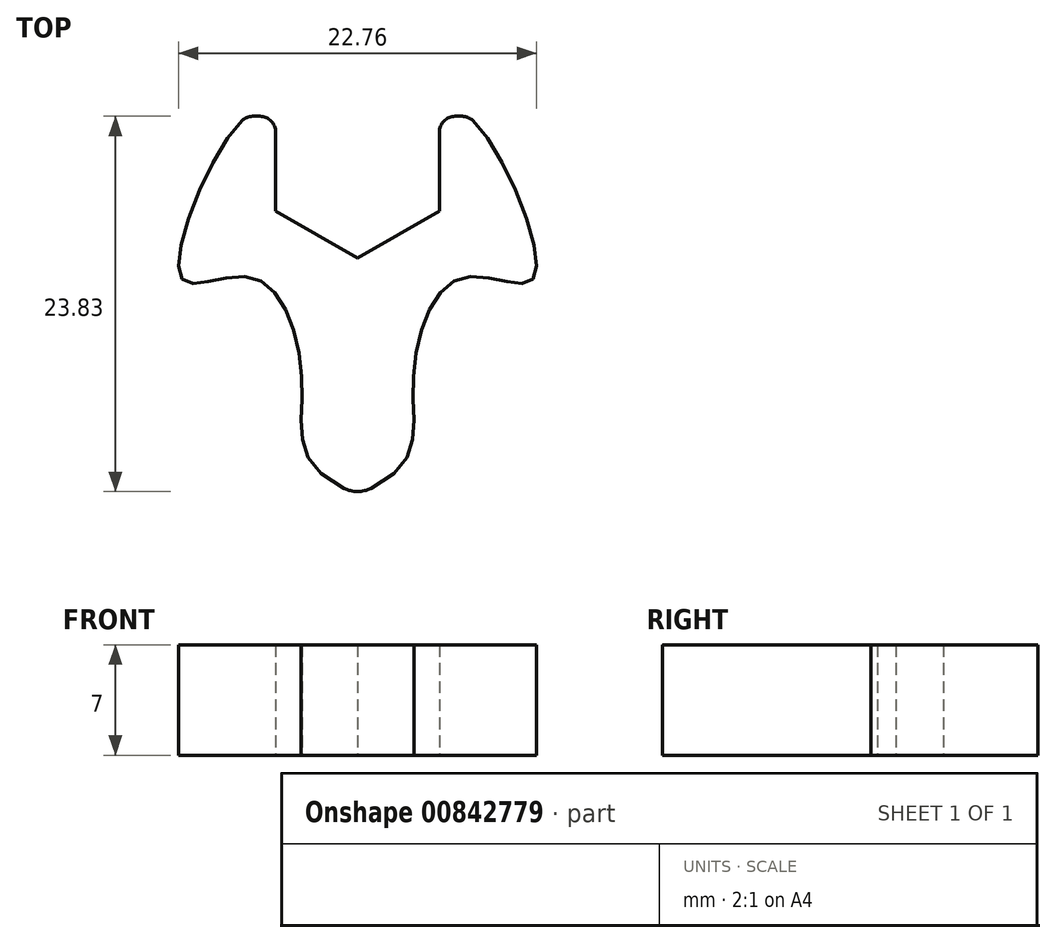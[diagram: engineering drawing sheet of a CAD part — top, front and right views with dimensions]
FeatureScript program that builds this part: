
annotation { "Feature Type Name" : "Feature", "Feature Type Description" : "" }
export const myFeature = defineFeature(function(context is Context, id is Id, definition is map)
    precondition{}
    {
        {
            var Q0;
            Q0=qCreatedBy(makeId("Top.planeOp"),FACE);
            var sketch = newSketch(context, id + "F0", { "sketchPlane" : qUnion([Q0])});
            skCircle(sketch, "E0.cCircle", {"center": v(0, 0) * mm, "radius": 5 * mm, "construction": true});
            skLineSegment(sketch, "E0.0", {"start": v(0, 5.77) * mm, "end": v(5, 2.89) * mm, "construction": true});
            skLineSegment(sketch, "E0.1", {"start": v(5, 2.89) * mm, "end": v(5, -2.89) * mm, "construction": true});
            skLineSegment(sketch, "E0.2", {"start": v(5, -2.89) * mm, "end": v(0, -5.77) * mm, "construction": true});
            skLineSegment(sketch, "E0.3", {"start": v(0, -5.77) * mm, "end": v(-5, -2.89) * mm, "construction": true});
            skLineSegment(sketch, "E0.4", {"start": v(-5, -2.89) * mm, "end": v(-5, 2.89) * mm, "construction": true});
            skLineSegment(sketch, "E0.5", {"start": v(-5, 2.89) * mm, "end": v(0, 5.77) * mm, "construction": true});
            skPoint(sketch, "E0.0.midPoint", {"position": v(2.5, 4.33) * mm});
            skLineSegment(sketch, "E1.0", {"start": v(-5.2, -3) * mm, "end": v(-5.2, 3) * mm, "construction": true});
            skLineSegment(sketch, "E1.1", {"start": v(0, 6) * mm, "end": v(5.2, 3) * mm, "construction": true});
            skLineSegment(sketch, "E1.2", {"start": v(5.2, 3) * mm, "end": v(5.2, -3) * mm});
            skLineSegment(sketch, "E1.3", {"start": v(-5.2, 3) * mm, "end": v(0, 6) * mm, "construction": true});
            skLineSegment(sketch, "E1.4", {"start": v(5.2, -3) * mm, "end": v(0, -6) * mm});
            skLineSegment(sketch, "E1.5", {"start": v(0, -6) * mm, "end": v(-5.2, -3) * mm, "construction": true});
            skLineSegment(sketch, "E2", {"start": v(11.2, -7.25) * mm, "end": v(6.7, -7.25) * mm, "construction": true});
            skLineSegment(sketch, "E3", {"start": v(6.7, -7.25) * mm, "end": v(0, -14.1) * mm, "construction": true});
            skLineSegment(sketch, "E4", {"start": v(5.2, 3) * mm, "end": v(7, 3) * mm});
            skLineSegment(sketch, "E5", {"start": v(7, 3) * mm, "end": v(11.2, -7.25) * mm, "construction": true});
            skFitSpline(sketch, "E6", {"points": [v(5.2, 3) * mm, v(7, 3) * mm, v(11.2, -7.25) * mm, v(6.7, -7.25) * mm, v(3.53, -14.1) * mm, v(0, -21) * mm], "startDerivative": vector(9.76, 6.58) * mm, "endDerivative": vector(-58.42, -22.32) * mm});
            skLineSegment(sketch, "E7", {"start": v(0, -21) * mm, "end": v(0, -6) * mm});
            skSolve(sketch);
        }
        {
            var Q0;
            Q0=makeQuery(id+"F0.imprint","IMPRINT",FACE,{"disambiguationData":[TD([[makeQuery(id+"F0.imprint","IMPRINT",EDGE,{"derivedFrom":sQuery(id+"F0.wireOp",EDGE,"E1.2")}),1.0]])]});
            extrude(context, id + "F1", {"entities" : qUnion([Q0]), "depth" : 7 * mm, "offsetDistance" : 25 * mm});
        }
        {
            var Q0;
            Q0=makeQuery(id+"F1.opExtrude","SWEPT_EDGE",EDGE,{"disambiguationData":[OSD([sQuery(id+"F0.wireOp",EDGE,"E4"),sQuery(id+"F0.wireOp",EDGE,"E6")])]});
            var Q1;
            Q1=makeQuery(id+"F1.opExtrude","SWEPT_EDGE",EDGE,{"disambiguationData":[OSD([sQuery(id+"F0.wireOp",EDGE,"E1.2"),sQuery(id+"F0.wireOp",EDGE,"E4"),sQuery(id+"F0.wireOp",EDGE,"E6")])]});
            fillet(context, id + "F2", {"entities" : qUnion([Q0, Q1]), "radius" : 1 * mm, "tangentPropagation" : true, "allowEdgeOverflow" : false});
        }
        {
            var Q0;
            Q0=makeQuery(id+"F1.opExtrude","SWEPT_BODY",BODY,{"disambiguationData":[OSD([sQuery(id+"F0.wireOp",EDGE,"E1.2"),sQuery(id+"F0.wireOp",EDGE,"E1.4"),sQuery(id+"F0.wireOp",EDGE,"E4"),sQuery(id+"F0.wireOp",EDGE,"E6"),sQuery(id+"F0.wireOp",EDGE,"E7")])]});
            var Q1;
            Q1=qCreatedBy(makeId("Right.planeOp"),FACE);
            mirror(context, id + "F3", {"operationType" : NewBodyOperationType.ADD, "entities" : qUnion([Q0]), "mirrorPlane" : qUnion([Q1])});
        }
        {
            var Q0;
            {var subQ0=makeQuery(id+"F1.opExtrude","SWEPT_EDGE",EDGE,{"disambiguationData":[OSD([sQuery(id+"F0.wireOp",EDGE,"E6"),sQuery(id+"F0.wireOp",EDGE,"E7")])]});Q0=makeQuery(id+"F3.boolean.opBoolean","MERGE",EDGE,{"derivedFrom":[subQ0,makeQuery(id+"F3.opPattern","COPY",EDGE,{"derivedFrom":subQ0,"instanceName":"1"})]});}
            fillet(context, id + "F4", {"entities" : qUnion([Q0]), "radius" : 2 * mm, "tangentPropagation" : true, "allowEdgeOverflow" : false});
        }
    });
